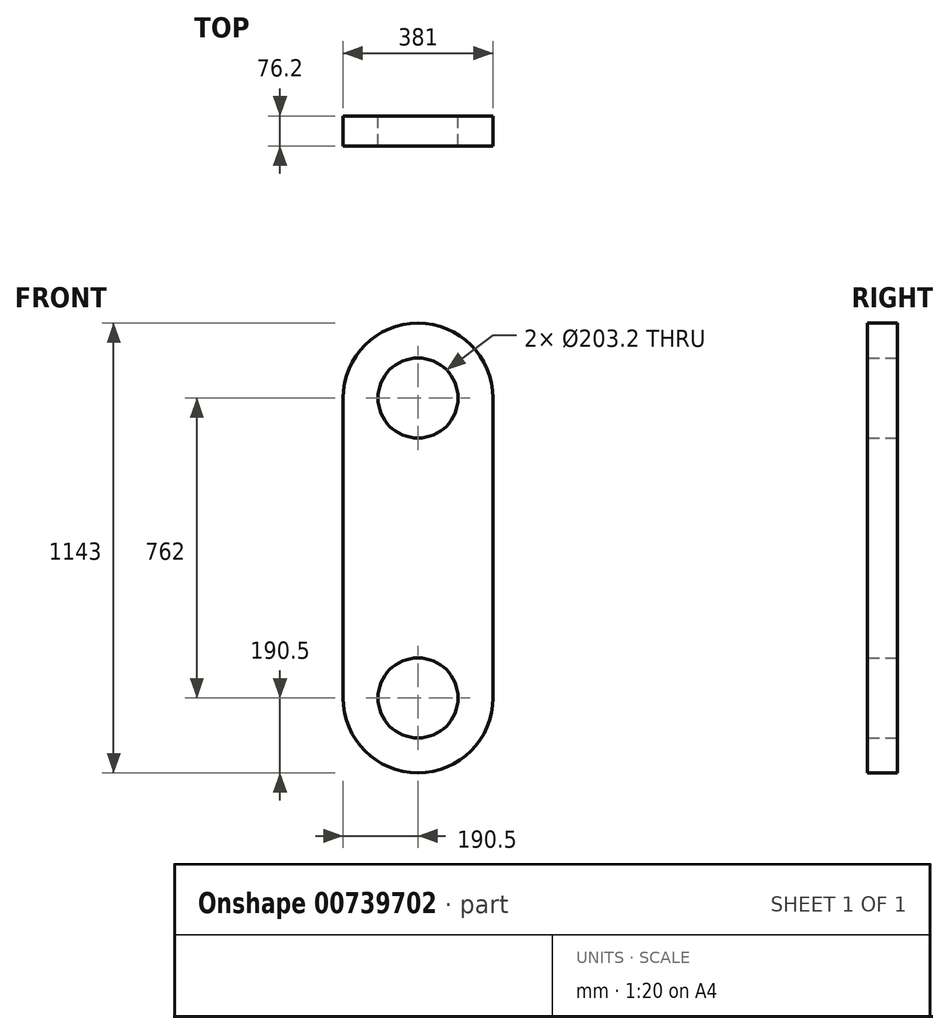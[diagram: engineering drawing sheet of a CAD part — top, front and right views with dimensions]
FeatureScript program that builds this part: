
annotation { "Feature Type Name" : "Feature", "Feature Type Description" : "" }
export const myFeature = defineFeature(function(context is Context, id is Id, definition is map)
    precondition{}
    {
        {
            var Q0;
            Q0=qCreatedBy(makeId("Front.planeOp"),FACE);
            var sketch = newSketch(context, id + "F0", { "sketchPlane" : qUnion([Q0])});
            skLineSegment(sketch, "E0.bottom", {"start": v(0, -190.5) * mm, "end": v(0, -190.5) * mm});
            skLineSegment(sketch, "E0.top", {"start": v(0, 952.5) * mm, "end": v(0, 952.5) * mm});
            skLineSegment(sketch, "E0.left", {"start": v(-190.5, 0) * mm, "end": v(-190.5, 762) * mm});
            skLineSegment(sketch, "E0.right", {"start": v(190.5, 0) * mm, "end": v(190.5, 762) * mm});
            skPoint(sketch, "E1.visualSharp", {"position": v(-190.5, 952.5) * mm});
            skArc(sketch, "E1.filletArc", {"start": v(0, 952.5) * mm, "mid": v(-134.7, 896.7) * mm, "end": v(-190.5, 762) * mm});
            skPoint(sketch, "E2.visualSharp", {"position": v(-190.5, -190.5) * mm});
            skArc(sketch, "E2.filletArc", {"start": v(-190.5, 0) * mm, "mid": v(-134.7, -134.7) * mm, "end": v(0, -190.5) * mm});
            skPoint(sketch, "E3.visualSharp", {"position": v(190.5, -190.5) * mm});
            skArc(sketch, "E3.filletArc", {"start": v(0, -190.5) * mm, "mid": v(134.7, -134.7) * mm, "end": v(190.5, 0) * mm});
            skPoint(sketch, "E4.visualSharp", {"position": v(190.5, 952.5) * mm});
            skArc(sketch, "E4.filletArc", {"start": v(190.5, 762) * mm, "mid": v(134.7, 896.7) * mm, "end": v(0, 952.5) * mm});
            skCircle(sketch, "E5", {"center": v(0, 762) * mm, "radius": 101.6 * mm});
            skCircle(sketch, "E6", {"center": v(0, 0) * mm, "radius": 101.6 * mm});
            skSolve(sketch);
        }
        {
            var Q0;
            Q0 = qSketchRegion(id + "F0", true);
            extrude(context, id + "F1", {"entities" : qUnion([Q0]), "depth" : 76.2 * mm, "offsetDistance" : 25.4 * mm});
        }
    });
